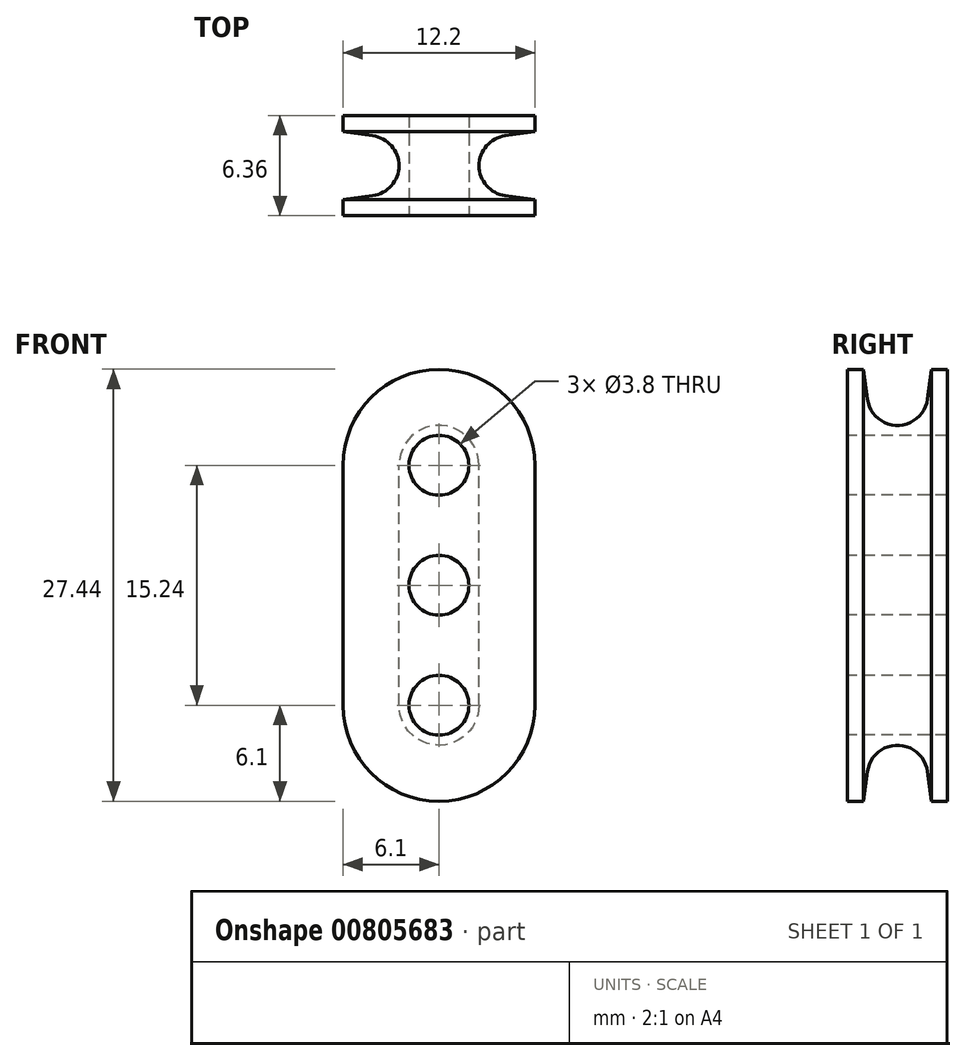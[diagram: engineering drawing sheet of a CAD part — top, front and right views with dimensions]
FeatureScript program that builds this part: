
annotation { "Feature Type Name" : "Feature", "Feature Type Description" : "" }
export const myFeature = defineFeature(function(context is Context, id is Id, definition is map)
    precondition{}
    {
        {
            var Q0;
            Q0=qCreatedBy(makeId("Front.planeOp"),FACE);
            var sketch = newSketch(context, id + "F0", { "sketchPlane" : qUnion([Q0])});
            skCircle(sketch, "E0", {"center": v(0, 0) * mm, "radius": 6.1 * mm});
            skSolve(sketch);
        }
        {
            var Q0;
            Q0=makeQuery(id+"F0.imprint","IMPRINT",FACE,{"disambiguationData":[TD([[makeQuery(id+"F0.imprint","IMPRINT",EDGE,{"derivedFrom":sQuery(id+"F0.wireOp",EDGE,"E0")}),1.0]])]});
            extrude(context, id + "F1", {"entities" : qUnion([Q0]), "depth" : 6.35 * mm, "offsetDistance" : 25.4 * mm, "symmetric" : true});
        }
        {
            var Q0;
            Q0=qCreatedBy(makeId("Front.planeOp"),FACE);
            var sketch = newSketch(context, id + "F2", { "sketchPlane" : qUnion([Q0])});
            skLineSegment(sketch, "E1.bottom", {"start": v(12.6, 0) * mm, "end": v(-13.53, 0) * mm});
            skLineSegment(sketch, "E1.top", {"start": v(12.6, -24.15) * mm, "end": v(-13.53, -24.15) * mm});
            skLineSegment(sketch, "E1.left", {"start": v(12.6, 0) * mm, "end": v(12.6, -24.15) * mm});
            skLineSegment(sketch, "E1.right", {"start": v(-13.53, 0) * mm, "end": v(-13.53, -24.15) * mm});
            skSolve(sketch);
        }
        {
            var Q0;
            Q0=qSketchRegion(id+"F2",true);
            extrude(context, id + "F3", {"entities" : qUnion([Q0]), "operationType" : NewBodyOperationType.REMOVE, "oppositeDirection" : true, "depth" : 25.4 * mm, "offsetDistance" : 25.4 * mm, "symmetric" : true});
        }
        {
            var Q0;
            Q0=makeQuery(id+"F1.opExtrude","CAP_FACE",FACE,{"disambiguationData":[OSD([sQuery(id+"F0.wireOp",EDGE,"E0")])],"isStart":false});
            var sketch = newSketch(context, id + "F4", { "sketchPlane" : qUnion([Q0])});
            skCircle(sketch, "E2", {"center": v(0, 0) * mm, "radius": 1.9 * mm});
            skSolve(sketch);
        }
        {
            var Q0;
            {var subQ0=makeQuery(id+"F8.boolean.opBoolean","MERGE",FACE,{"derivedFrom":[makeQuery(id+"F1.opExtrude","CAP_FACE",FACE,{"disambiguationData":[OSD([sQuery(id+"F0.wireOp",EDGE,"E0")])],"isStart":false}),makeQuery(id+"F8.opExtrude","SWEPT_FACE",FACE,{"disambiguationData":[OSD([sQuery(id+"FHCKBcZkIibrD3C_1.wireOp",EDGE,"33893b92-1531-43ea-a95e-b28fcb7d8d0e.6")])]})]});Q0=makeQuery(id+"F9.boolean.opBoolean","MERGE",FACE,{"derivedFrom":[subQ0,makeQuery(id+"F9.opPattern","COPY",FACE,{"derivedFrom":subQ0,"instanceName":"1"})]});}
            extrude(context, id + "F5", {"entities" : qUnion([Q0]), "operationType" : NewBodyOperationType.ADD, "depth" : 3.17 * mm - 1.02 * mm, "offsetDistance" : 25.4 * mm});
        }
        {
            var Q0;
            Q0=qCreatedBy(makeId("Right.planeOp"),FACE);
            var sketch = newSketch(context, id + "F6", { "sketchPlane" : qUnion([Q0])});
            skLineSegment(sketch, "E3", {"start": v(2.41, 7.99) * mm, "end": v(1.9, 4.2) * mm});
            skLineSegment(sketch, "E4", {"start": v(-2.41, 7.99) * mm, "end": v(-1.9, 4.2) * mm});
            skLineSegment(sketch, "E5", {"start": v(2.41, 7.99) * mm, "end": v(-2.41, 7.99) * mm});
            skArc(sketch, "E6", {"start": v(-1.9, 4.2) * mm, "mid": v(0, 2.54) * mm, "end": v(1.9, 4.2) * mm});
            skLineSegment(sketch, "E7", {"start": v(11.1, 0) * mm, "end": v(0, 0) * mm, "construction": true});
            skPoint(sketch, "E8", {"position": v(0, 2.54) * mm});
            skLineSegment(sketch, "E9", {"start": v(0, 0) * mm, "end": v(0, 4.46) * mm, "construction": true});
            skLineSegment(sketch, "E10.0", {"start": v(3.18, 0) * mm, "end": v(3.18, 6.1) * mm, "construction": true});
            skPoint(sketch, "E11", {"position": v(2.16, 6.1) * mm});
            skPoint(sketch, "E12", {"position": v(-2.16, 6.1) * mm});
            skLineSegment(sketch, "E13.1.0.0", {"start": v(-2.92, 7.99) * mm, "end": v(-3.43, 4.2) * mm});
            skLineSegment(sketch, "E13.direction1", {"start": v(-1.9, 4.2) * mm, "end": v(-7.24, 4.2) * mm, "construction": true});
            skPoint(sketch, "E14", {"position": v(-3.18, 6.1) * mm});
            skLineSegment(sketch, "E15", {"start": v(2.16, 6.1) * mm, "end": v(3.18, 6.1) * mm, "construction": true});
            skLineSegment(sketch, "E16", {"start": v(-3.18, 6.1) * mm, "end": v(-2.16, 6.1) * mm, "construction": true});
            skArc(sketch, "E17", {"start": v(-3.43, 4.2) * mm, "mid": v(-3.68, 3.74) * mm, "end": v(-4.17, 3.56) * mm});
            skLineSegment(sketch, "E18", {"start": v(-4.17, 3.56) * mm, "end": v(-5.95, 3.56) * mm});
            skLineSegment(sketch, "E19", {"start": v(-5.95, 3.56) * mm, "end": v(-5.95, 7.99) * mm});
            skLineSegment(sketch, "E20", {"start": v(-5.95, 7.99) * mm, "end": v(-2.92, 7.99) * mm});
            skSolve(sketch);
        }
        {
            var Q0;
            Q0=makeQuery(id+"F6.imprint","IMPRINT",FACE,{"disambiguationData":[TD([[makeQuery(id+"F6.imprint","IMPRINT",EDGE,{"derivedFrom":sQuery(id+"F6.wireOp",EDGE,"E3")}),-1.0]])]});
            var Q1;
            Q1=makeQuery(id+"F6.imprint","IMPRINT",FACE,{"disambiguationData":[TD([[makeQuery(id+"F6.imprint","IMPRINT",EDGE,{"derivedFrom":sQuery(id+"F6.wireOp",EDGE,"E13.1.0.0")}),-1.0]])]});
            var Q2;
            Q2=sQuery(id+"F6.wireOp",EDGE,"E7");
            var Q3;
            Q3=sQuery(id+"F6.wireOp",EDGE,"E7");
            revolve(context, id + "F7", {"operationType" : NewBodyOperationType.REMOVE, "surfaceOperationType" : NewSurfaceOperationType.NEW, "entities" : qUnion([Q0, Q1]), "surfaceEntities" : qUnion([Q2]), "axis" : qUnion([Q3]), "revolveType" : RevolveType.FULL, "oppositeDirection" : true});
        }
        {
            var Q0;
            {var subQ0=sQuery(id+"F2.wireOp",EDGE,"E1.bottom");Q0=makeQuery(id+"F5.boolean.opBoolean","MERGE",FACE,{"derivedFrom":[makeQuery(id+"F3.boolean.opBoolean","COPY",FACE,{"derivedFrom":makeQuery(id+"F3.opExtrude","SWEPT_FACE",FACE,{"disambiguationData":[OSD([subQ0])]})}),makeQuery(id+"F5.opExtrude","SWEPT_FACE",FACE,{"disambiguationData":[OSD([sQuery(id+"F0.wireOp",EDGE,"E0"),subQ0])]})]});}
            extrude(context, id + "F8", {"entities" : qUnion([Q0]), "operationType" : NewBodyOperationType.ADD, "depth" : 7.62 * mm, "offsetDistance" : 25.4 * mm});
        }
        {
            var Q0;
            Q0=makeQuery(id+"F1.opExtrude","SWEPT_BODY",BODY,{"disambiguationData":[OSD([sQuery(id+"F0.wireOp",EDGE,"E0")])]});
            var Q1;
            Q1=makeQuery(id+"F8.opExtrude","CAP_FACE",FACE,{"disambiguationData":[OSD([sQuery(id+"F0.wireOp",EDGE,"E0"),sQuery(id+"F2.wireOp",EDGE,"E1.bottom")])],"isStart":false});
            mirror(context, id + "F9", {"operationType" : NewBodyOperationType.ADD, "entities" : qUnion([Q0]), "mirrorPlane" : qUnion([Q1])});
        }
        {
            var Q0;
            Q0=qSketchRegion(id+"F4",true);
            extrude(context, id + "F10", {"entities" : qUnion([Q0]), "operationType" : NewBodyOperationType.REMOVE, "oppositeDirection" : true, "depth" : 127 * mm, "offsetDistance" : 25.4 * mm, "symmetric" : true});
        }
        {
            var Q0;
            {var subQ0=sQuery(id+"F2.wireOp",EDGE,"E1.bottom");var subQ1=sQuery(id+"F0.wireOp",EDGE,"E0");var subQ2=makeQuery(id+"F8.boolean.opBoolean","MERGE",FACE,{"derivedFrom":[makeQuery(id+"F5.opExtrude","CAP_FACE",FACE,{"disambiguationData":[OSD([subQ1])],"isStart":false}),makeQuery(id+"F8.opExtrude","SWEPT_FACE",FACE,{"disambiguationData":[OSD([subQ1,subQ0]),TDD([makeQuery(id+"F5.opExtrude","CAP_EDGE",EDGE,{"disambiguationData":[OSD([subQ1,subQ0])],"isStart":false})])]})]});Q0=makeQuery(id+"F9.boolean.opBoolean","MERGE",FACE,{"derivedFrom":[subQ2,makeQuery(id+"F9.opPattern","COPY",FACE,{"derivedFrom":subQ2,"instanceName":"1"})]});}
            var sketch = newSketch(context, id + "F11", { "sketchPlane" : qUnion([Q0])});
            skCircle(sketch, "E21.0", {"center": v(0, 0) * mm, "radius": 1.9 * mm});
            skCircle(sketch, "E22.0.1.0", {"center": v(0, -7.62) * mm, "radius": 1.9 * mm});
            skCircle(sketch, "E22.0.2.0", {"center": v(0, -15.24) * mm, "radius": 1.9 * mm});
            skLineSegment(sketch, "E22.direction1", {"start": v(0, 0) * mm, "end": v(25.4, 0) * mm, "construction": true});
            skLineSegment(sketch, "E22.direction2", {"start": v(0, 0) * mm, "end": v(0, -7.62) * mm, "construction": true});
            skSolve(sketch);
        }
        {
            var Q0;
            Q0=makeQuery(id+"F11.imprint","IMPRINT",FACE,{"disambiguationData":[TD([[makeQuery(id+"F11.imprint","IMPRINT",EDGE,{"derivedFrom":sQuery(id+"F11.wireOp",EDGE,"E22.0.1.0")}),1.0]])]});
            var Q1;
            Q1=makeQuery(id+"F11.imprint","IMPRINT",FACE,{"disambiguationData":[TD([[makeQuery(id+"F11.imprint","IMPRINT",EDGE,{"derivedFrom":sQuery(id+"F11.wireOp",EDGE,"E22.0.2.0")}),1.0]])]});
            extrude(context, id + "F12", {"entities" : qUnion([Q0, Q1]), "operationType" : NewBodyOperationType.REMOVE, "endBound" : BoundingType.THROUGH_ALL, "oppositeDirection" : true, "depth" : 25.4 * mm, "offsetDistance" : 25.4 * mm});
        }
        {
            var Q0;
            Q0=qCreatedBy(makeId("Right.planeOp"),FACE);
            var sketch = newSketch(context, id + "F13", { "sketchPlane" : qUnion([Q0])});
            skLineSegment(sketch, "E23.bottom", {"start": v(-3.18, 10.31) * mm, "end": v(-10.8, 10.31) * mm});
            skLineSegment(sketch, "E23.top", {"start": v(-3.17, -24.1) * mm, "end": v(-10.8, -24.1) * mm});
            skLineSegment(sketch, "E23.left", {"start": v(-3.18, 10.31) * mm, "end": v(-3.17, -24.1) * mm});
            skLineSegment(sketch, "E23.right", {"start": v(-10.8, 10.31) * mm, "end": v(-10.8, -24.1) * mm});
            skSolve(sketch);
        }
        {
            var Q0;
            Q0 = qSketchRegion(id + "F13", true);
            extrude(context, id + "F14", {"entities" : qUnion([Q0]), "operationType" : NewBodyOperationType.REMOVE, "depth" : 127 * mm, "offsetDistance" : 25.4 * mm, "symmetric" : true});
        }
    });
